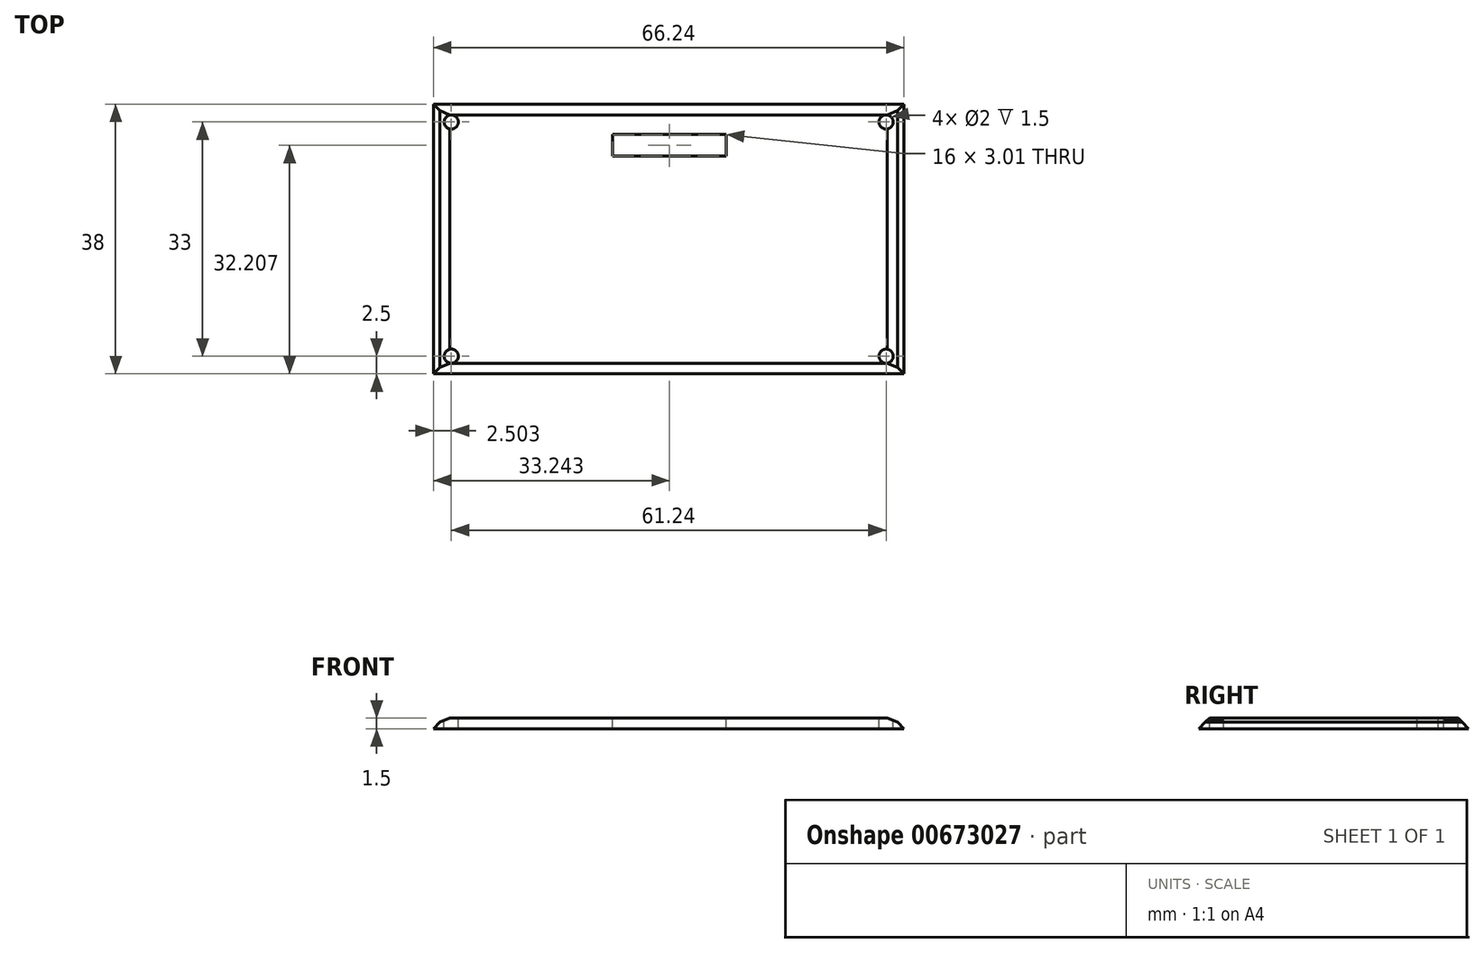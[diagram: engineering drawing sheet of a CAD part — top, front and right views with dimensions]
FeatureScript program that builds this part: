
annotation { "Feature Type Name" : "Feature", "Feature Type Description" : "" }
export const myFeature = defineFeature(function(context is Context, id is Id, definition is map)
    precondition{}
    {
        {
            var Q0;
            Q0=qCreatedBy(makeId("Top.planeOp"),FACE);
            var sketch = newSketch(context, id + "F0", { "sketchPlane" : qUnion([Q0])});
            skLineSegment(sketch, "E0.bottom", {"start": v(-21.06, -4.4) * mm, "end": v(46.18, -4.4) * mm});
            skLineSegment(sketch, "E0.top", {"start": v(-21.06, -43.4) * mm, "end": v(46.18, -43.4) * mm});
            skLineSegment(sketch, "E0.left", {"start": v(-21.06, -4.4) * mm, "end": v(-21.06, -43.4) * mm});
            skLineSegment(sketch, "E0.right", {"start": v(46.18, -4.4) * mm, "end": v(46.18, -43.4) * mm});
            skSolve(sketch);
        }
        {
            var Q0;
            Q0 = qSketchRegion(id + "F0", true);
            extrude(context, id + "F1", {"entities" : qUnion([Q0]), "depth" : 1.5 * mm, "offsetDistance" : 25 * mm});
        }
        {
            var Q0;
            Q0=makeQuery(id+"F1.opExtrude","CAP_EDGE",EDGE,{"disambiguationData":[OSD([sQuery(id+"F0.wireOp",EDGE,"E0.right")])],"isStart":false});
            var Q1;
            Q1=makeQuery(id+"F1.opExtrude","CAP_EDGE",EDGE,{"disambiguationData":[OSD([sQuery(id+"F0.wireOp",EDGE,"E0.left")])],"isStart":false});
            chamfer(context, id + "F2", {"entities" : qUnion([Q0, Q1]), "width" : 2 * mm, "tangentPropagation" : true});
        }
        {
            var Q0;
            Q0=makeQuery(id+"F1.opExtrude","CAP_EDGE",EDGE,{"disambiguationData":[OSD([sQuery(id+"F0.wireOp",EDGE,"E0.bottom")])],"isStart":false});
            var Q1;
            Q1=makeQuery(id+"F1.opExtrude","CAP_FACE",FACE,{"disambiguationData":[OSD([sQuery(id+"F0.wireOp",EDGE,"E0.bottom"),sQuery(id+"F0.wireOp",EDGE,"E0.top"),sQuery(id+"F0.wireOp",EDGE,"E0.left"),sQuery(id+"F0.wireOp",EDGE,"E0.right")])],"isStart":false});
            chamfer(context, id + "F3", {"entities" : qUnion([Q0, Q1]), "width" : 2 * mm, "tangentPropagation" : true});
        }
        {
            var Q0;
            Q0=makeQuery(id+"F1.opExtrude","CAP_FACE",FACE,{"disambiguationData":[OSD([sQuery(id+"F0.wireOp",EDGE,"E0.bottom"),sQuery(id+"F0.wireOp",EDGE,"E0.top"),sQuery(id+"F0.wireOp",EDGE,"E0.left"),sQuery(id+"F0.wireOp",EDGE,"E0.right")])],"isStart":false});
            var sketch = newSketch(context, id + "F4", { "sketchPlane" : qUnion([Q0])});
            skCircle(sketch, "E1", {"center": v(43.18, -40.4) * mm, "radius": 1 * mm});
            skCircle(sketch, "E2", {"center": v(43.18, -7.4) * mm, "radius": 1 * mm});
            skCircle(sketch, "E3", {"center": v(-18.06, -40.4) * mm, "radius": 1 * mm});
            skCircle(sketch, "E4", {"center": v(-18.06, -7.4) * mm, "radius": 1 * mm});
            skSolve(sketch);
        }
        {
            var Q0;
            Q0 = qSketchRegion(id + "F4", true);
            extrude(context, id + "F5", {"entities" : qUnion([Q0]), "operationType" : NewBodyOperationType.REMOVE, "oppositeDirection" : true, "depth" : 2 * mm, "offsetDistance" : 25 * mm});
        }
        {
            var Q0;
            {var subQ0=sQuery(id+"F0.wireOp",EDGE,"E0.right");var subQ1=sQuery(id+"F0.wireOp",EDGE,"E0.left");var subQ2=sQuery(id+"F0.wireOp",EDGE,"E0.top");var subQ3=sQuery(id+"F0.wireOp",EDGE,"E0.bottom");var subQ4=makeQuery(id+"F1.opExtrude","CAP_FACE",FACE,{"disambiguationData":[OSD([subQ3,subQ2,subQ1,subQ0])],"isStart":false});Q0=makeQuery(id+"F5.boolean.opBoolean","SPLIT",FACE,{"disambiguationData":[TD([subQ4,makeQuery(id+"F3.opChamfer","BLEND_FACE",FACE,{"disambiguationData":[OSD([subQ3])]}),makeQuery(id+"F3.opChamfer","BLEND_FACE",FACE,{"disambiguationData":[OSD([subQ2])]}),makeQuery(id+"F3.opChamfer","BLEND_FACE",FACE,{"disambiguationData":[OSD([subQ3,subQ2,subQ1,subQ0]),TDD([makeQuery(id+"F2.opChamfer","BLEND_EDGE",EDGE,{"blendedFrom":[makeQuery(id+"F1.opExtrude","CAP_EDGE",EDGE,{"disambiguationData":[OSD([subQ1])],"isStart":false}),subQ4],"blendedInto":[subQ4]})])]}),makeQuery(id+"F3.opChamfer","BLEND_FACE",FACE,{"disambiguationData":[OSD([subQ3,subQ2,subQ1,subQ0]),TDD([makeQuery(id+"F2.opChamfer","BLEND_EDGE",EDGE,{"blendedFrom":[makeQuery(id+"F1.opExtrude","CAP_EDGE",EDGE,{"disambiguationData":[OSD([subQ0])],"isStart":false}),subQ4],"blendedInto":[subQ4]})])]}),makeQuery(id+"F5.opExtrude","SWEPT_FACE",FACE,{"disambiguationData":[OSD([sQuery(id+"F4.wireOp",EDGE,"E1")])]}),makeQuery(id+"F5.opExtrude","SWEPT_FACE",FACE,{"disambiguationData":[OSD([sQuery(id+"F4.wireOp",EDGE,"E2")])]}),makeQuery(id+"F5.opExtrude","SWEPT_FACE",FACE,{"disambiguationData":[OSD([sQuery(id+"F4.wireOp",EDGE,"E3")])]}),makeQuery(id+"F5.opExtrude","SWEPT_FACE",FACE,{"disambiguationData":[OSD([sQuery(id+"F4.wireOp",EDGE,"E4")])]})])],"derivedFrom":subQ4});}
            var sketch = newSketch(context, id + "F6", { "sketchPlane" : qUnion([Q0])});
            skLineSegment(sketch, "E5.bottom", {"start": v(4.68, -12.2) * mm, "end": v(20.68, -12.2) * mm});
            skLineSegment(sketch, "E5.top", {"start": v(4.68, -9.2) * mm, "end": v(20.68, -9.2) * mm});
            skLineSegment(sketch, "E5.left", {"start": v(4.68, -12.2) * mm, "end": v(4.68, -9.2) * mm});
            skLineSegment(sketch, "E5.right", {"start": v(20.68, -12.2) * mm, "end": v(20.68, -9.2) * mm});
            skSolve(sketch);
        }
        {
            var Q0;
            Q0 = qSketchRegion(id + "F6", true);
            extrude(context, id + "F7", {"entities" : qUnion([Q0]), "operationType" : NewBodyOperationType.REMOVE, "oppositeDirection" : true, "depth" : 2 * mm, "offsetDistance" : 25 * mm});
        }
    });
